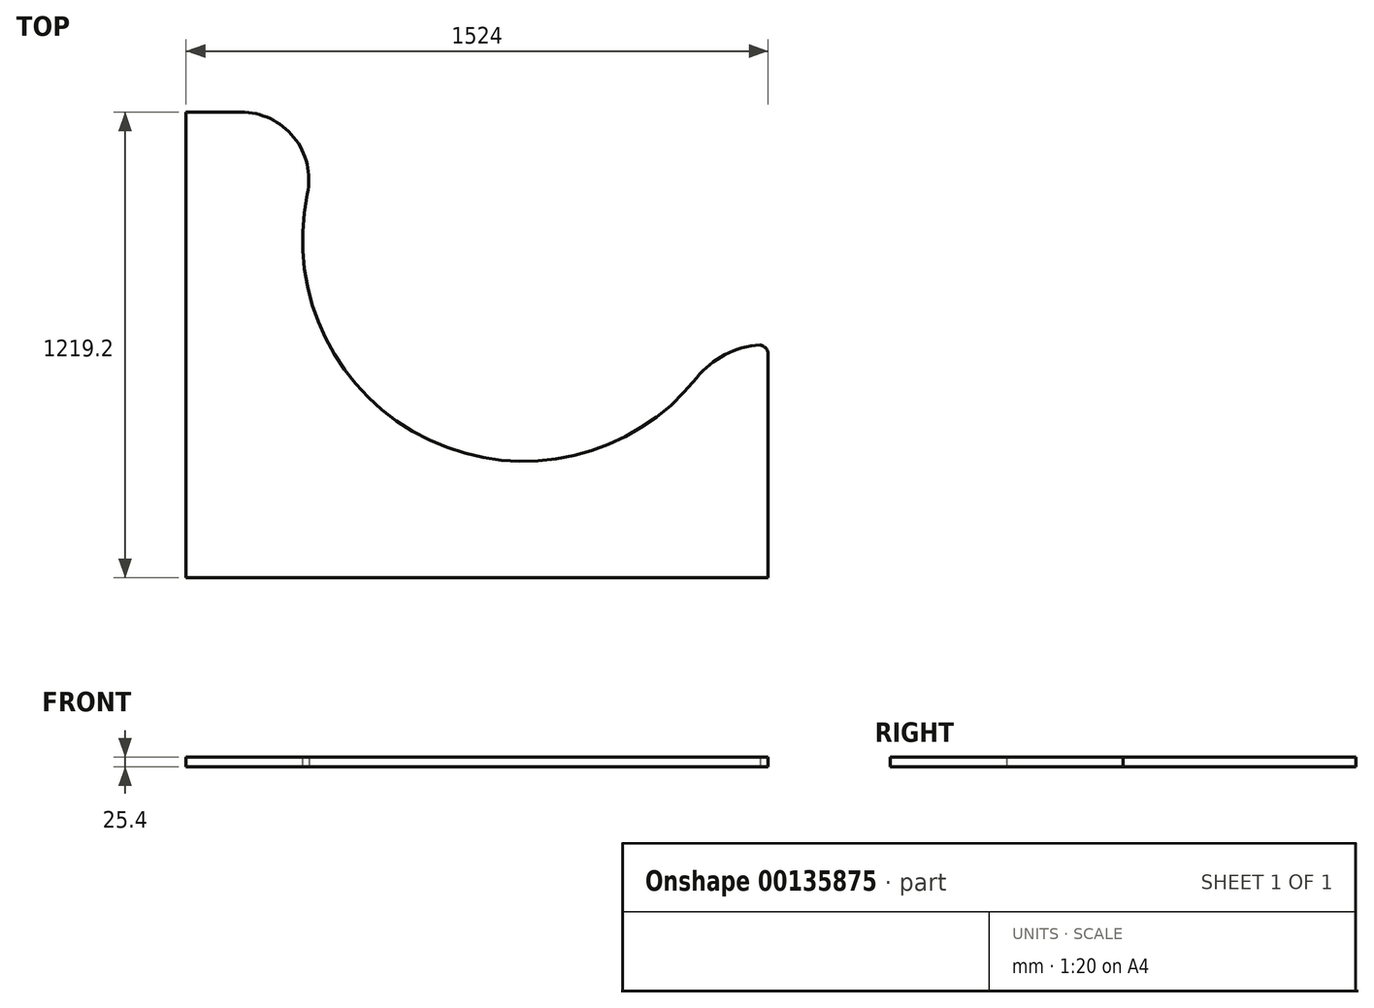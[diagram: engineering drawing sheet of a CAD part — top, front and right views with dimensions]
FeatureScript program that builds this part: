
annotation { "Feature Type Name" : "Feature", "Feature Type Description" : "" }
export const myFeature = defineFeature(function(context is Context, id is Id, definition is map)
    precondition{}
    {
        {
            var Q0;
            Q0=qCreatedBy(makeId("Top.planeOp"),FACE);
            var sketch = newSketch(context, id + "F0", { "sketchPlane" : qUnion([Q0])});
            skLineSegment(sketch, "E0.bottom", {"start": v(762, -609.6) * mm, "end": v(-762, -609.6) * mm});
            skLineSegment(sketch, "E0.top", {"start": v(-618.44, 609.6) * mm, "end": v(-762, 609.6) * mm});
            skLineSegment(sketch, "E0.left", {"start": v(762, -609.6) * mm, "end": v(762, 609.6) * mm});
            skLineSegment(sketch, "E0.right", {"start": v(-762, -609.6) * mm, "end": v(-762, 609.6) * mm});
            skPoint(sketch, "E0.middle", {"position": v(0, 0) * mm});
            skLineSegment(sketch, "E1", {"start": v(-762, -609.6) * mm, "end": v(121.92, -609.6) * mm});
            skLineSegment(sketch, "E2", {"start": v(121.92, -609.6) * mm, "end": v(121.92, 609.6) * mm});
            skPoint(sketch, "E2.endSnap0", {"position": v(0, 609.6) * mm});
            skLineSegment(sketch, "E3", {"start": v(121.92, 609.6) * mm, "end": v(121.92, 274.32) * mm});
            skArc(sketch, "E4", {"start": v(-444.53, 394.8) * mm, "mid": v(-125.2, -249.43) * mm, "end": v(575.09, -86.26) * mm});
            skPoint(sketch, "E5.newPointB", {"position": v(762, 609.6) * mm});
            skArc(sketch, "E5.filletArc", {"start": v(-444.53, 394.8) * mm, "mid": v(-480.25, 543.68) * mm, "end": v(-618.44, 609.6) * mm});
            skLineSegment(sketch, "E6", {"start": v(762, -609.6) * mm, "end": v(762, -25.4) * mm});
            skLineSegment(sketch, "E7", {"start": v(753.97, 0) * mm, "end": v(736.6, 0) * mm});
            skPoint(sketch, "E8.visualSharp", {"position": v(631.95, 0) * mm});
            skArc(sketch, "E8.filletArc", {"start": v(753.97, 0) * mm, "mid": v(654.67, -22.7) * mm, "end": v(575.09, -86.26) * mm});
            skPoint(sketch, "E9.visualSharp", {"position": v(762, 0) * mm});
            skArc(sketch, "E9.filletArc", {"start": v(762, -25.4) * mm, "mid": v(754.56, -7.44) * mm, "end": v(736.6, 0) * mm});
            skSolve(sketch);
        }
        {
            var Q0;
            {var subQ4=sQuery(id+"F0.wireOp",EDGE,"E0.bottom");Q0=makeQuery(id+"F0.imprint","IMPRINT",FACE,{"disambiguationData":[TD([[makeQuery(id+"F0.imprint","IMPRINT",EDGE,{"derivedFrom":subQ4}),-1.0]])]});}
            var Q1;
            Q1=makeQuery(id+"F0.imprint","IMPRINT",FACE,{"disambiguationData":[TD([[makeQuery(id+"F0.imprint","IMPRINT",EDGE,{"derivedFrom":sQuery(id+"F0.wireOp",EDGE,"E0.top")}),1.0]])]});
            extrude(context, id + "F1", {"entities" : qUnion([Q0, Q1]), "depth" : 25.4 * mm});
        }
    });
